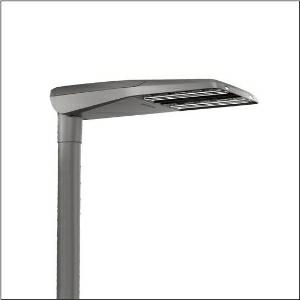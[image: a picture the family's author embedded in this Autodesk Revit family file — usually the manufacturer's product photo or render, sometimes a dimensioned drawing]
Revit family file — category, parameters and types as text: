
# Revit family: streetlight_sl_11_iq_midi___pc-r_5xc3f41e08me_ca65
name_source: partatom
category: Lighting Fixtures
units: mm (PartAtom-declared; Revit-internal decimal feet)

## family parameters
Cut with Voids When Loaded = No
Host = Face
Light Source = No
Part Type = Normal
Room Calculation Point = No
Round Connector Dimension = Use Diameter
Shared = No

## types (1)
- --- (1 x LED, 16220 lm, 124.7 W, 4000K)
    Apparent Load = 125 VA
    CIE Flux Codes = 37 73 96 100 100
    Color Rendering = 70
    Color Temperature = 4000K
    Default Elevation = 1800 mm
    Description = Streetlight SL 11 iQ midi, mast luminaire, primary light control with 3 zone facetted reflector, of plastic, silver coated, highly specular, primary optical cover: cover, of PMMA, transparent, light distribution: PC-R, light emission: direct distribution, primary light characteristic: asymmetric, installation type: post-top, side-entry, LED, High Power LED, rated luminous flux: 16.220lm, luminous efficacy: 130lm/W, light colour: 740, colour temperature: 4000K, control: optimised constant luminous flux control (CLO 2.0), Desk-Remote (wireless, voltage-free reading and setting of iQ features in the workshop via application-optimized NFC function/RFID function), Light-Fading, Smart-Wire, Night-Set, Lumen-Switch, Temp-Guard, Auto-Match, with cable H07RN-F 5x 1.5mm², mains connection: 220..240V, AC, 50/60Hz, connection cable pre-assembled, cable length: 12,5m, start of lifetime: 125W, end of lifetime: 132W, reduction: 61W, luminaire housing, of diecast aluminium, powder-coated, Siteco® metallic grey (DB 702S), length: 780mm, width: 376mm, height: 118mm, spigot size: 60/76mm (post-top) and 42/60/76mm (side-entry), mast flange for spigot size: 42mm: 5XC10008XM4, 60mm: 5XC10008XM2, 76/60mm: 5XC10108XM1, equipment: Power, protection rating (complete): IP66, insulation class (complete): insulation class II (safety insulation), certification: CE, ENEC, VDE, impact resistance: IK09, permissible operating ambient temperature for outdoor applications: -25..+50°C, standard-compliant lighting for roads and squares, packaging unit: 1 piece

Light Distribution: PC-R
    Height = 118 mm
    Lamp = 1 x LED
    Lamp Light Flux = 16220 lm
    Lamp Power = 124.7 W
    Lamp count = 1
    Length = 780 mm
    Luminous efficacy = 130 lm/W
    Manufacturer = Siteco
    ModVariant = No
    Model = 5XC3F41E08ME
    Number of Poles = 1
    OnlyDefault = Yes
    Power Factor = 1
    Product Name = Streetlight SL 11 iQ midi | PC-R
    Product group = mast luminaire | pylon top
    ProductGroupID = 6100
    Protection Class = Protection class II
    Protection Degree = IP 66
    RLX_Detail_Level = 1
    RlxData = <blob elided: 74125 chars, md5=255a4490>
    Socket = socket
    Standby Power = 0 W
    System Light Flux = 16220 lm
    System Power = 125 W
    Type Comments = factory setting: luminous flux: 100 % | dim-lin: 254 | 557 mA
    Type Image = l_1005960.jpg
    URL = http://relux.com
    VarID = @adj_117741
    Voltage = 0 V
    Weight = 0.00 kg
    Width = 376 mm

## geometry (parser evidence)
native form markers: Blend x4, Sweep x9
no freeform markers — native parametric forms only
